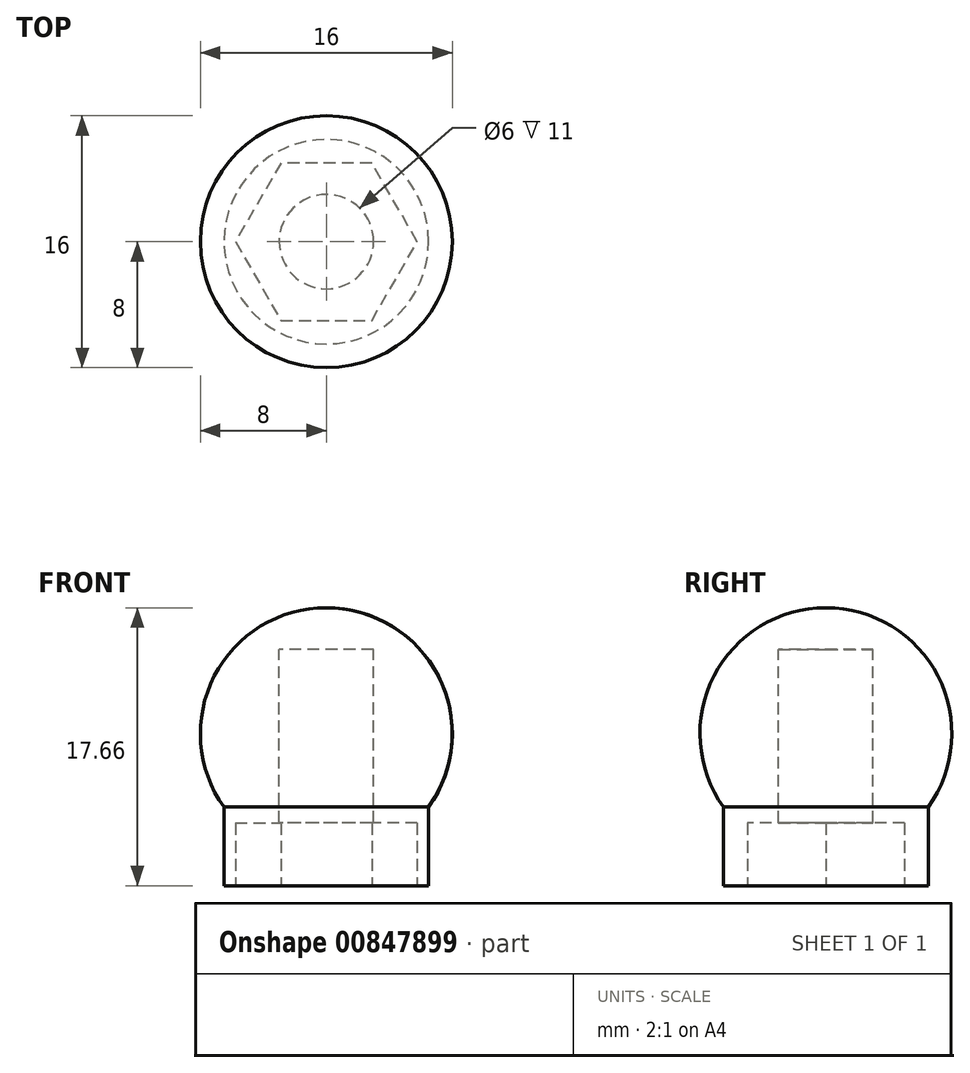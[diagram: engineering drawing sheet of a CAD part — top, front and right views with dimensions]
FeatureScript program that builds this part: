
annotation { "Feature Type Name" : "Feature", "Feature Type Description" : "" }
export const myFeature = defineFeature(function(context is Context, id is Id, definition is map)
    precondition{}
    {
        {
            var Q0;
            Q0=qCreatedBy(makeId("Front.planeOp"),FACE);
            var sketch = newSketch(context, id + "F0", { "sketchPlane" : qUnion([Q0])});
            skArc(sketch, "E0", {"start": v(3, -7.42) * mm, "mid": v(7.85, 1.53) * mm, "end": v(0, 8) * mm});
            skLineSegment(sketch, "E1.right", {"start": v(6.5, -4.66) * mm, "end": v(6.5, -9.66) * mm});
            skLineSegment(sketch, "E2.top", {"start": v(0, 5.34) * mm, "end": v(3, 5.34) * mm});
            skLineSegment(sketch, "E2.right", {"start": v(3, 5.34) * mm, "end": v(3, -9.66) * mm});
            skLineSegment(sketch, "E3.trimOffspring", {"start": v(3, -4.66) * mm, "end": v(6.5, -4.66) * mm});
            skLineSegment(sketch, "E4.trimOffspring", {"start": v(3, -9.66) * mm, "end": v(6.5, -9.66) * mm});
            skLineSegment(sketch, "E5", {"start": v(0, 13.42) * mm, "end": v(0, 0) * mm, "construction": true});
            skLineSegment(sketch, "E6", {"start": v(0, 8) * mm, "end": v(0, 5.34) * mm});
            skSolve(sketch);
        }
        {
            var Q0;
            {var subQ2=sQuery(id+"F0.wireOp",EDGE,"E2.top");Q0=makeQuery(id+"F0.imprint","IMPRINT",FACE,{"disambiguationData":[TD([[makeQuery(id+"F0.imprint","IMPRINT",EDGE,{"derivedFrom":subQ2}),1.0]])]});}
            var Q1;
            {var subQ3=sQuery(id+"F0.wireOp",EDGE,"E3.trimOffspring");Q1=makeQuery(id+"F0.imprint","IMPRINT",FACE,{"disambiguationData":[TD([[makeQuery(id+"F0.imprint","IMPRINT",EDGE,{"derivedFrom":subQ3}),-1.0]])]});}
            var Q2;
            {var subQ3=sQuery(id+"F0.wireOp",EDGE,"E1.right");Q2=makeQuery(id+"F0.imprint","IMPRINT",FACE,{"disambiguationData":[TD([[makeQuery(id+"F0.imprint","IMPRINT",EDGE,{"derivedFrom":subQ3}),-1.0]])]});}
            var Q3;
            Q3=sQuery(id+"F0.wireOp",EDGE,"E5");
            revolve(context, id + "F1", {"surfaceOperationType" : NewSurfaceOperationType.NEW, "entities" : qUnion([Q0, Q1, Q2]), "axis" : qUnion([Q3]), "revolveType" : RevolveType.FULL});
        }
        {
            var Q0;
            Q0=makeQuery(id+"F1.opRevolve","SWEPT_FACE",FACE,{"disambiguationData":[OSD([sQuery(id+"F0.wireOp",EDGE,"E4.trimOffspring")])]});
            var sketch = newSketch(context, id + "F2", { "sketchPlane" : qUnion([Q0])});
            skCircle(sketch, "E7.cCircle", {"center": v(0, 0) * mm, "radius": 5 * mm, "construction": true});
            skLineSegment(sketch, "E7.0", {"start": v(-5.77, 0) * mm, "end": v(-2.89, 5) * mm});
            skLineSegment(sketch, "E7.1", {"start": v(-2.89, 5) * mm, "end": v(2.89, 5) * mm});
            skLineSegment(sketch, "E7.2", {"start": v(2.89, 5) * mm, "end": v(5.77, 0) * mm});
            skLineSegment(sketch, "E7.3", {"start": v(5.77, 0) * mm, "end": v(2.89, -5) * mm});
            skLineSegment(sketch, "E7.4", {"start": v(2.89, -5) * mm, "end": v(-2.89, -5) * mm});
            skLineSegment(sketch, "E7.5", {"start": v(-2.89, -5) * mm, "end": v(-5.77, 0) * mm});
            skPoint(sketch, "E7.0.midPoint", {"position": v(-4.33, 2.5) * mm});
            skSolve(sketch);
        }
        {
            var Q0;
            Q0=makeQuery(id+"F2.imprint","IMPRINT",FACE,{"disambiguationData":[TD([[makeQuery(id+"F2.imprint","IMPRINT",EDGE,{"derivedFrom":sQuery(id+"F2.wireOp",EDGE,"E7.0")}),-1.0]])]});
            extrude(context, id + "F3", {"entities" : qUnion([Q0]), "operationType" : NewBodyOperationType.REMOVE, "oppositeDirection" : true, "depth" : 4 * mm, "offsetDistance" : 25 * mm});
        }
    });
